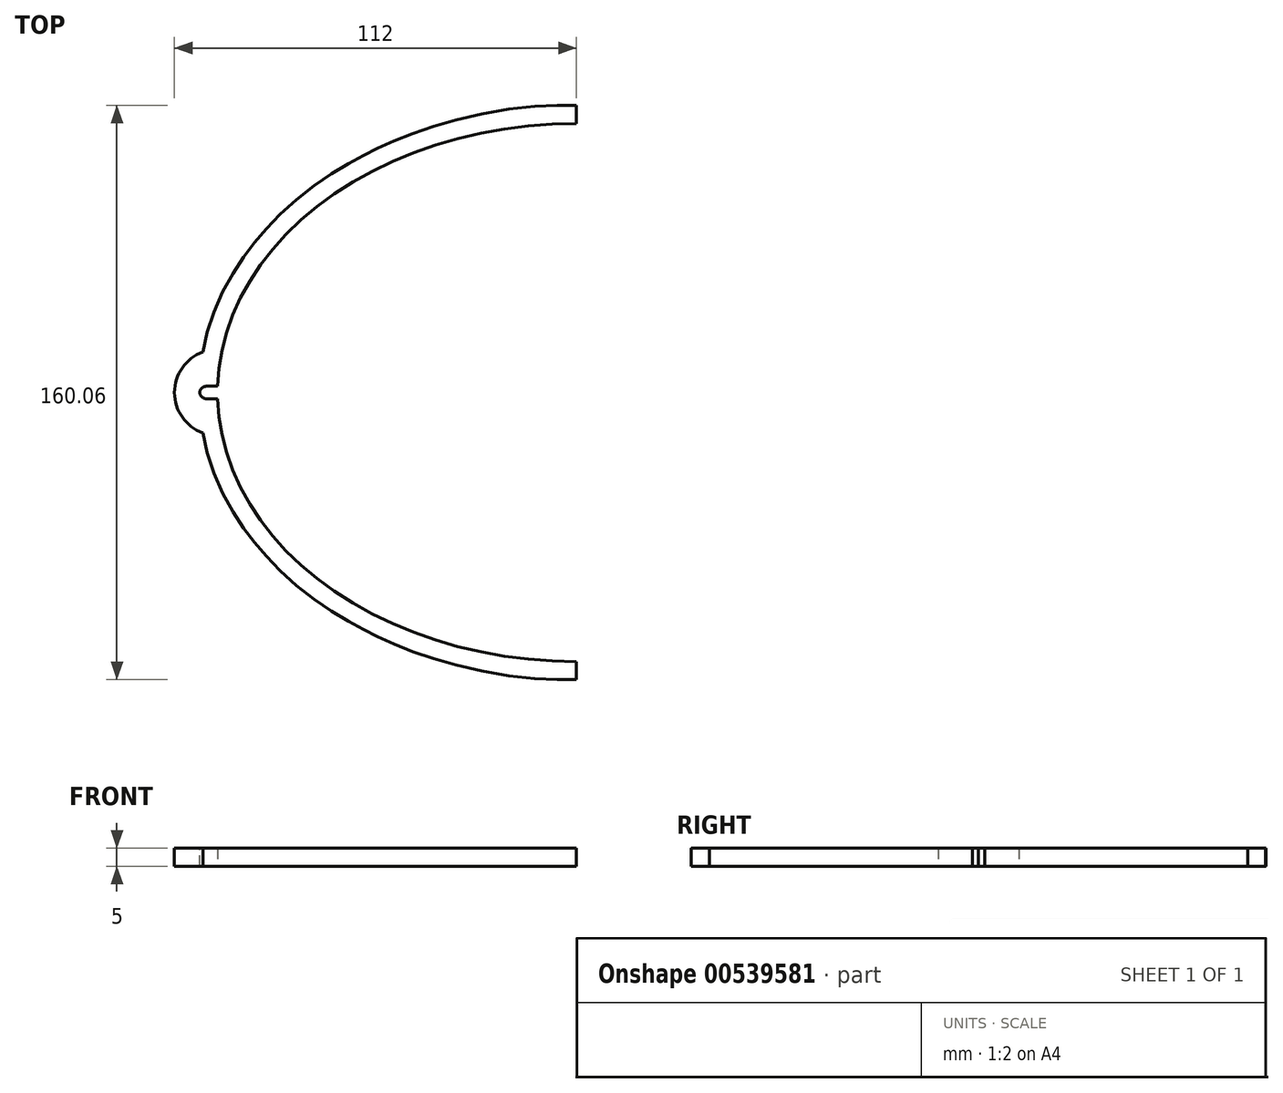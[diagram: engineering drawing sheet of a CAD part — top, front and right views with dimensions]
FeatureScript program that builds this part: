
annotation { "Feature Type Name" : "Feature", "Feature Type Description" : "" }
export const myFeature = defineFeature(function(context is Context, id is Id, definition is map)
    precondition{}
    {
        {
            var Q0;
            Q0=qCreatedBy(makeId("Top.planeOp"),FACE);
            var sketch = newSketch(context, id + "F0", { "sketchPlane" : qUnion([Q0])});
            skEllipticalArc(sketch, "E0", {});
            skFitSpline(sketch, "E1.0", {"points": [v(0, 80) * mm, v(-6.83, 80) * mm, v(-17, 79.24) * mm, v(-30.17, 76.77) * mm, v(-39.78, 74.2) * mm, v(-47.5, 71.46) * mm, v(-53.5, 68.91) * mm, v(-57.84, 66.85) * mm, v(-62.05, 64.62) * mm, v(-67.46, 61.45) * mm, v(-73.82, 57.13) * mm, v(-80.78, 51.37) * mm, v(-85.96, 46.14) * mm, v(-89.7, 41.7) * mm, v(-93.18, 37.11) * mm, v(-96.93, 31.15) * mm, v(-100.5, 23.68) * mm, v(-103.08, 15.96) * mm, v(-104.38, 9.36) * mm, v(-104.91, 4.03) * mm, v(-105.04, 0) * mm, v(-104.91, -4.03) * mm, v(-104.38, -9.36) * mm, v(-103.08, -15.96) * mm, v(-100.5, -23.68) * mm, v(-96.93, -31.15) * mm, v(-93.18, -37.11) * mm, v(-89.7, -41.7) * mm, v(-85.96, -46.14) * mm, v(-80.78, -51.37) * mm, v(-73.82, -57.13) * mm, v(-67.46, -61.45) * mm, v(-62.05, -64.62) * mm, v(-57.84, -66.85) * mm, v(-53.5, -68.91) * mm, v(-47.5, -71.46) * mm, v(-39.78, -74.2) * mm, v(-30.17, -76.77) * mm, v(-17, -79.24) * mm, v(-6.83, -80) * mm, v(0, -80) * mm]});
            skLineSegment(sketch, "E2", {"start": v(0, 75) * mm, "end": v(0, 80) * mm});
            skLineSegment(sketch, "E3", {"start": v(0, -75) * mm, "end": v(0, -80) * mm});
            const initialGuessF0  = {"E0": [0, 0, 1, 0, 0.1, 0.075, 1.5707963267948966, 4.71238898038469]};
            skSetInitialGuess(sketch, initialGuessF0);
            skSolve(sketch);
        }
        {
            var Q0;
            Q0=makeQuery(id+"F0.imprint","IMPRINT",FACE,{"disambiguationData":[TD([[makeQuery(id+"F0.imprint","IMPRINT",EDGE,{"derivedFrom":sQuery(id+"F0.wireOp",EDGE,"E0")}),-1.0]])]});
            extrude(context, id + "F1", {"entities" : qUnion([Q0]), "depth" : 5 * mm, "offsetDistance" : 25 * mm});
        }
        {
            var Q0;
            Q0=makeQuery(id+"F1.opExtrude","CAP_FACE",FACE,{"disambiguationData":[OSD([sQuery(id+"F0.wireOp",EDGE,"E0"),sQuery(id+"F0.wireOp",EDGE,"E1.0"),sQuery(id+"F0.wireOp",EDGE,"E2"),sQuery(id+"F0.wireOp",EDGE,"E3")])],"isStart":false});
            var sketch = newSketch(context, id + "F2", { "sketchPlane" : qUnion([Q0])});
            skArc(sketch, "E4", {"start": v(-98.73, 11.93) * mm, "mid": v(-112, 0) * mm, "end": v(-98.73, -11.93) * mm});
            skLineSegment(sketch, "E5", {"start": v(-98.73, 11.93) * mm, "end": v(-98.73, -11.93) * mm});
            skSolve(sketch);
        }
        {
            var Q0;
            {var subQ0=sQuery(id+"F2.wireOp",EDGE,"E4");var subQ1=makeQuery(id+"F1.opExtrude","CAP_EDGE",EDGE,{"disambiguationData":[OSD([sQuery(id+"F0.wireOp",EDGE,"E1.0")])],"isStart":false});var subQ2=makeQuery(id+"F2.imprint","INTERSECT",VERTEX,{"disambiguationData":[OD(0.0)],"derivedFrom":[subQ1,subQ0]});Q0=makeQuery(id+"F2.imprint","IMPRINT",FACE,{"disambiguationData":[TD([[makeQuery(id+"F2.imprint","IMPRINT",EDGE,{"disambiguationData":[TD([[subQ2,-1.0]])],"derivedFrom":subQ0}),1.0]])]});}
            var Q1;
            {var subQ1=sQuery(id+"F2.wireOp",EDGE,"E4");var subQ4=makeQuery(id+"F1.opExtrude","CAP_EDGE",EDGE,{"disambiguationData":[OSD([sQuery(id+"F0.wireOp",EDGE,"E1.0")])],"isStart":false});var subQ5=makeQuery(id+"F2.imprint","INTERSECT",VERTEX,{"disambiguationData":[OD(0.0)],"derivedFrom":[subQ4,subQ1]});Q1=makeQuery(id+"F2.imprint","IMPRINT",FACE,{"disambiguationData":[TD([[makeQuery(id+"F2.imprint","IMPRINT",EDGE,{"disambiguationData":[TD([[subQ5,-1.0]])],"derivedFrom":subQ4}),1.0]])]});}
            extrude(context, id + "F3", {"entities" : qUnion([Q0, Q1]), "operationType" : NewBodyOperationType.ADD, "oppositeDirection" : true, "depth" : 5 * mm, "offsetDistance" : 25 * mm});
        }
        {
            var Q0;
            {var subQ0=sQuery(id+"F0.wireOp",EDGE,"E0");Q0=makeQuery(id+"F3.boolean.opBoolean","MERGE",FACE,{"derivedFrom":[makeQuery(id+"F1.opExtrude","CAP_FACE",FACE,{"disambiguationData":[OSD([subQ0,sQuery(id+"F0.wireOp",EDGE,"E1.0"),sQuery(id+"F0.wireOp",EDGE,"E2"),sQuery(id+"F0.wireOp",EDGE,"E3")])],"isStart":false}),makeQuery(id+"F3.opExtrude","CAP_FACE",FACE,{"disambiguationData":[OSD([subQ0,sQuery(id+"F2.wireOp",EDGE,"E4")])],"isStart":true})]});}
            var sketch = newSketch(context, id + "F4", { "sketchPlane" : qUnion([Q0])});
            skLineSegment(sketch, "E6.bottom", {"start": v(-95, -1.75) * mm, "end": v(-105, -1.75) * mm});
            skLineSegment(sketch, "E6.top", {"start": v(-95, 1.75) * mm, "end": v(-105, 1.75) * mm});
            skLineSegment(sketch, "E6.left", {"start": v(-95, -1.75) * mm, "end": v(-95, 1.75) * mm});
            skLineSegment(sketch, "E6.right", {"start": v(-105, -1.75) * mm, "end": v(-105, 1.75) * mm});
            skPoint(sketch, "E6.middle", {"position": v(-100, 0) * mm});
            skSolve(sketch);
        }
        {
            var Q0;
            {var subQ0=sQuery(id+"F4.wireOp",EDGE,"E6.right");Q0=makeQuery(id+"F4.imprint","IMPRINT",FACE,{"disambiguationData":[TD([[makeQuery(id+"F4.imprint","IMPRINT",EDGE,{"derivedFrom":subQ0}),-1.0]])]});}
            var Q1;
            {var subQ0=sQuery(id+"F4.wireOp",EDGE,"E6.left");Q1=makeQuery(id+"F4.imprint","IMPRINT",FACE,{"disambiguationData":[TD([[makeQuery(id+"F4.imprint","IMPRINT",EDGE,{"derivedFrom":subQ0}),1.0]])]});}
            extrude(context, id + "F5", {"entities" : qUnion([Q0, Q1]), "operationType" : NewBodyOperationType.REMOVE, "oppositeDirection" : true, "depth" : 25 * mm, "offsetDistance" : 25 * mm});
        }
        {
            var Q0;
            Q0=makeQuery(id+"F5.boolean.opBoolean","COPY",EDGE,{"derivedFrom":makeQuery(id+"F5.opExtrude","SWEPT_EDGE",EDGE,{"disambiguationData":[OSD([sQuery(id+"F4.wireOp",EDGE,"E6.top"),sQuery(id+"F4.wireOp",EDGE,"E6.right")])]})});
            var Q1;
            Q1=makeQuery(id+"F5.boolean.opBoolean","COPY",EDGE,{"derivedFrom":makeQuery(id+"F5.opExtrude","SWEPT_EDGE",EDGE,{"disambiguationData":[OSD([sQuery(id+"F4.wireOp",EDGE,"E6.bottom"),sQuery(id+"F4.wireOp",EDGE,"E6.right")])]})});
            fillet(context, id + "F6", {"entities" : qUnion([Q0, Q1]), "radius" : 2 * mm, "tangentPropagation" : true, "allowEdgeOverflow" : false});
        }
    });
